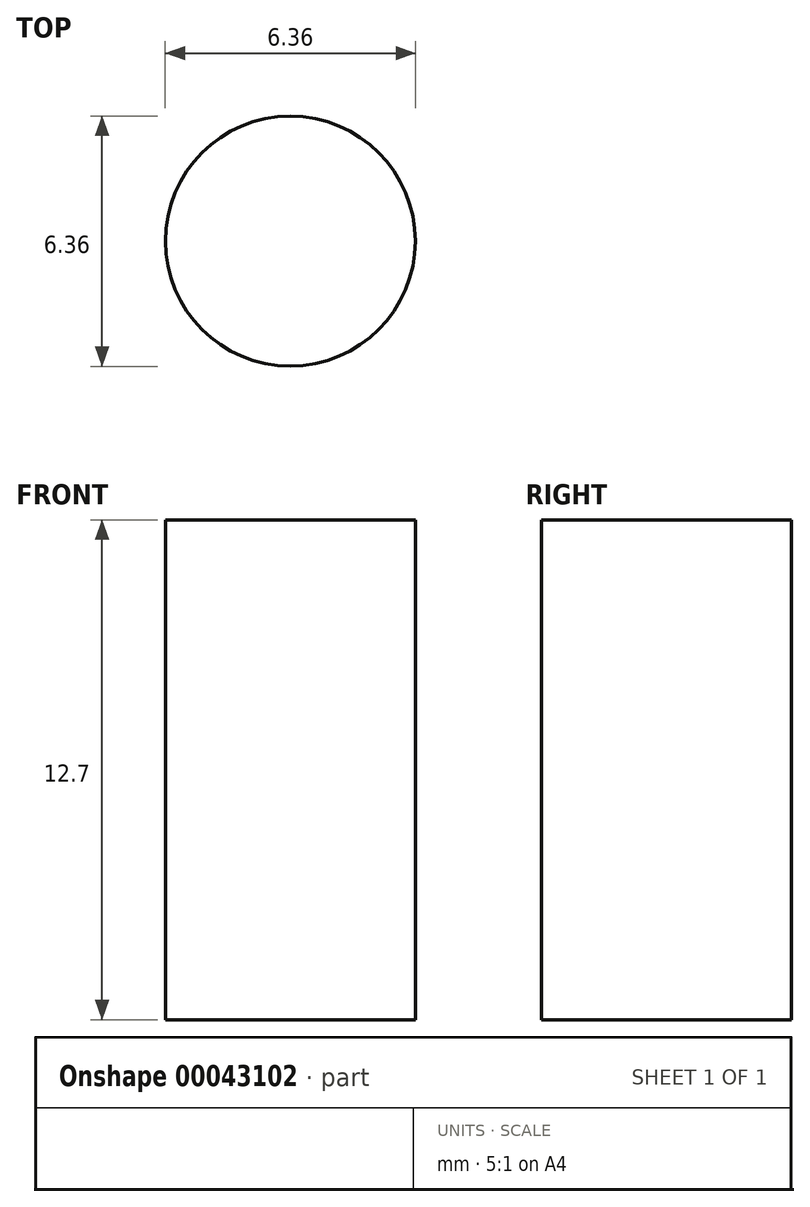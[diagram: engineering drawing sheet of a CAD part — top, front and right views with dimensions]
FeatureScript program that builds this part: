
annotation { "Feature Type Name" : "Feature", "Feature Type Description" : "" }
export const myFeature = defineFeature(function(context is Context, id is Id, definition is map)
    precondition{}
    {
        {
            var Q0;
            Q0=qCreatedBy(makeId("Top.planeOp"),FACE);
            var sketch = newSketch(context, id + "F0", { "sketchPlane" : qUnion([Q0])});
            skCircle(sketch, "E0", {"center": v(0, 0) * mm, "radius": 3.18 * mm});
            skSolve(sketch);
        }
        {
            var Q0;
            Q0 = qSketchRegion(id + "F0", true);
            extrude(context, id + "F1", {"entities" : qUnion([Q0]), "depth" : 12.7 * mm});
        }
    });
